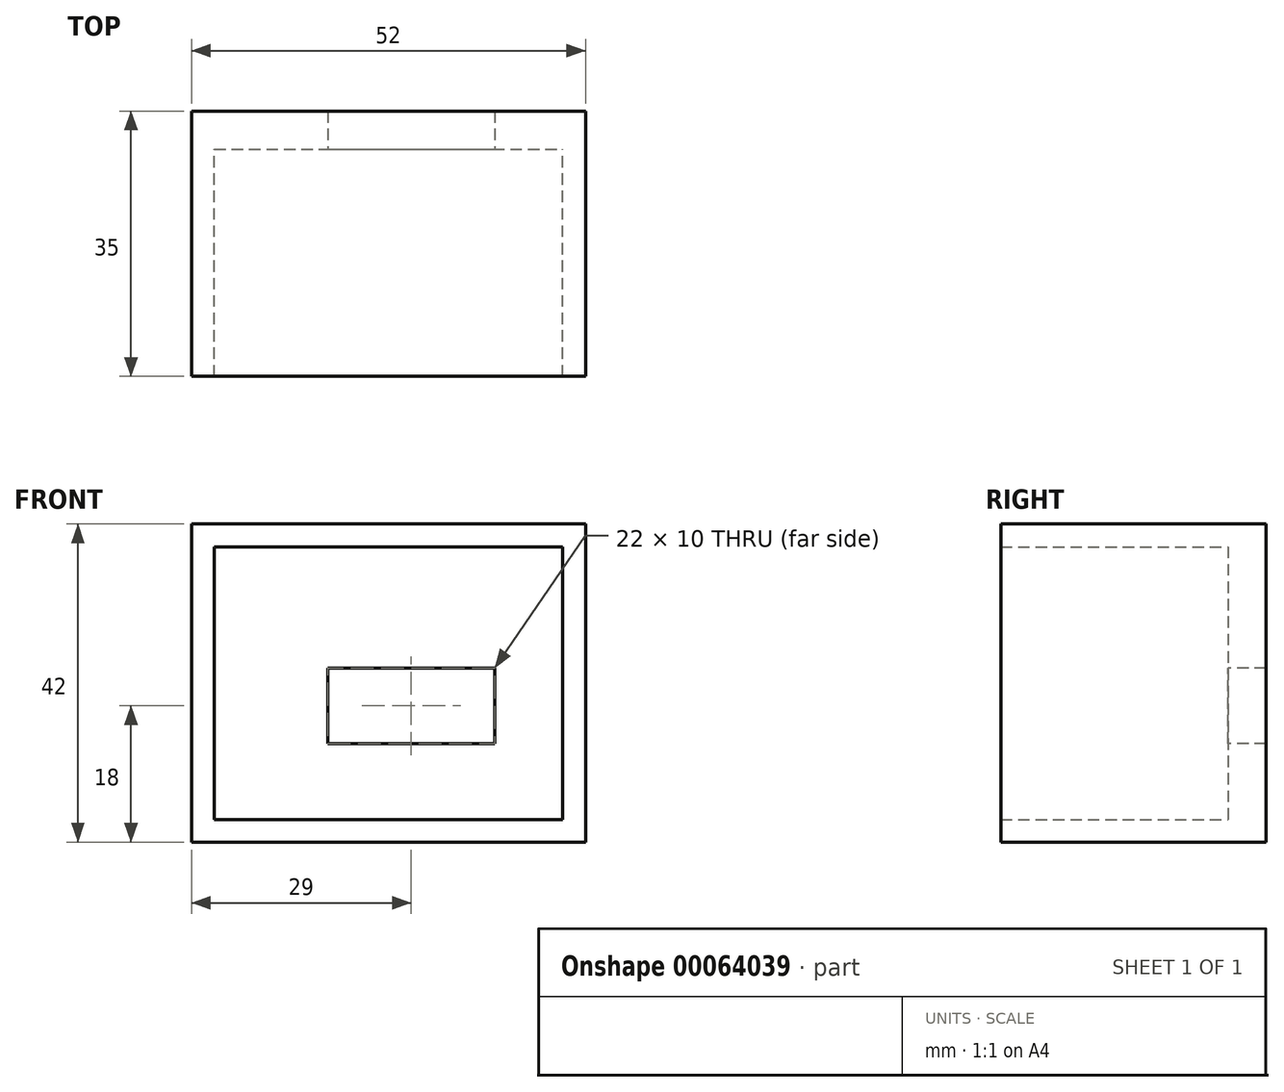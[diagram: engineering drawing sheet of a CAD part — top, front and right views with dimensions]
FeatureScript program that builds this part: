
annotation { "Feature Type Name" : "Feature", "Feature Type Description" : "" }
export const myFeature = defineFeature(function(context is Context, id is Id, definition is map)
    precondition{}
    {
        {
            var Q0;
            Q0=qCreatedBy(makeId("Front.planeOp"),FACE);
            var sketch = newSketch(context, id + "F0", { "sketchPlane" : qUnion([Q0])});
            skLineSegment(sketch, "E0.bottom", {"start": v(0, 36) * mm, "end": v(46, 36) * mm});
            skLineSegment(sketch, "E0.top", {"start": v(0, 0) * mm, "end": v(46, 0) * mm});
            skLineSegment(sketch, "E0.left", {"start": v(0, 36) * mm, "end": v(0, 0) * mm});
            skLineSegment(sketch, "E0.right", {"start": v(46, 36) * mm, "end": v(46, 0) * mm});
            skLineSegment(sketch, "E1.bottom", {"start": v(15, 10) * mm, "end": v(37, 10) * mm});
            skLineSegment(sketch, "E1.top", {"start": v(15, 20) * mm, "end": v(37, 20) * mm});
            skLineSegment(sketch, "E1.left", {"start": v(15, 10) * mm, "end": v(15, 20) * mm});
            skLineSegment(sketch, "E1.right", {"start": v(37, 10) * mm, "end": v(37, 20) * mm});
            skLineSegment(sketch, "E2.bottom", {"start": v(-3, 39) * mm, "end": v(49, 39) * mm});
            skLineSegment(sketch, "E2.top", {"start": v(-3, -3) * mm, "end": v(49, -3) * mm});
            skLineSegment(sketch, "E2.left", {"start": v(-3, 39) * mm, "end": v(-3, -3) * mm});
            skLineSegment(sketch, "E2.right", {"start": v(49, 39) * mm, "end": v(49, -3) * mm});
            skSolve(sketch);
        }
        {
            var Q0;
            Q0=makeQuery(id+"F0.imprint","IMPRINT",FACE,{"disambiguationData":[TD([[makeQuery(id+"F0.imprint","IMPRINT",EDGE,{"derivedFrom":sQuery(id+"F0.wireOp",EDGE,"E0.bottom")}),-1.0]])]});
            var Q1;
            Q1=makeQuery(id+"F0.imprint","IMPRINT",FACE,{"disambiguationData":[TD([[makeQuery(id+"F0.imprint","IMPRINT",EDGE,{"derivedFrom":sQuery(id+"F0.wireOp",EDGE,"E0.bottom")}),1.0]])]});
            extrude(context, id + "F1", {"entities" : qUnion([Q0, Q1]), "oppositeDirection" : true, "depth" : 5 * mm});
        }
        {
            var Q0;
            Q0=makeQuery(id+"F0.imprint","IMPRINT",FACE,{"disambiguationData":[TD([[makeQuery(id+"F0.imprint","IMPRINT",EDGE,{"derivedFrom":sQuery(id+"F0.wireOp",EDGE,"E0.bottom")}),1.0]])]});
            extrude(context, id + "F2", {"entities" : qUnion([Q0]), "operationType" : NewBodyOperationType.ADD, "depth" : 30 * mm});
        }
    });
